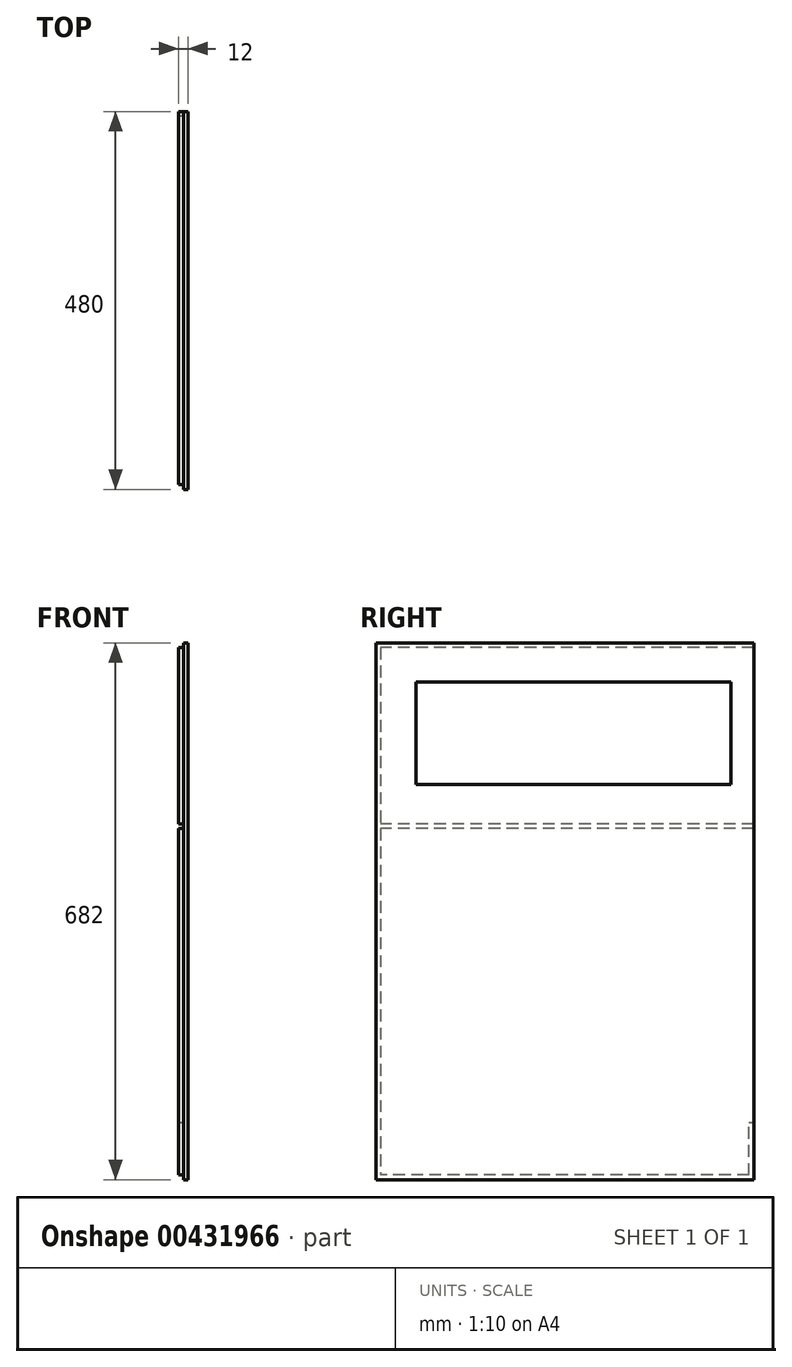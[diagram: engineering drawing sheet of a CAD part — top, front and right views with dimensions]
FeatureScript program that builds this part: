
annotation { "Feature Type Name" : "Feature", "Feature Type Description" : "" }
export const myFeature = defineFeature(function(context is Context, id is Id, definition is map)
    precondition{}
    {
        {
            var Q0;
            Q0=qCreatedBy(makeId("Right.planeOp"),FACE);
            var sketch = newSketch(context, id + "F0", { "sketchPlane" : qUnion([Q0])});
            skLineSegment(sketch, "E0.bottom", {"start": v(-240, 341) * mm, "end": v(240, 341) * mm});
            skLineSegment(sketch, "E0.top", {"start": v(-240, -341) * mm, "end": v(240, -341) * mm});
            skLineSegment(sketch, "E0.left", {"start": v(-240, 341) * mm, "end": v(-240, -341) * mm});
            skLineSegment(sketch, "E0.right", {"start": v(240, 341) * mm, "end": v(240, -341) * mm});
            skPoint(sketch, "E0.middle", {"position": v(0, 0) * mm});
            skSolve(sketch);
        }
        {
            var Q0;
            Q0=makeQuery(id+"F0.imprint","IMPRINT",FACE,{"disambiguationData":[TD([[makeQuery(id+"F0.imprint","IMPRINT",EDGE,{"derivedFrom":sQuery(id+"F0.wireOp",EDGE,"E0.bottom")}),-1.0]])]});
            extrude(context, id + "F1", {"entities" : qUnion([Q0]), "depth" : 12 * mm, "offsetDistance" : 25 * mm});
        }
        {
            var Q0;
            Q0=makeQuery(id+"F1.opExtrude","CAP_FACE",FACE,{"disambiguationData":[OSD([sQuery(id+"F0.wireOp",EDGE,"E0.bottom"),sQuery(id+"F0.wireOp",EDGE,"E0.top"),sQuery(id+"F0.wireOp",EDGE,"E0.left"),sQuery(id+"F0.wireOp",EDGE,"E0.right")])],"isStart":true});
            var sketch = newSketch(context, id + "F2", { "sketchPlane" : qUnion([Q0])});
            skLineSegment(sketch, "E1.bottom", {"start": v(240, 341) * mm, "end": v(234, 341) * mm});
            skLineSegment(sketch, "E1.top", {"start": v(240, -341) * mm, "end": v(234, -341) * mm});
            skLineSegment(sketch, "E1.left", {"start": v(240, 341) * mm, "end": v(240, -341) * mm});
            skLineSegment(sketch, "E1.right", {"start": v(234, 341) * mm, "end": v(234, -341) * mm});
            skSolve(sketch);
        }
        {
            var Q0;
            Q0=qSketchRegion(id+"F2",true);
            extrude(context, id + "F3", {"entities" : qUnion([Q0]), "operationType" : NewBodyOperationType.REMOVE, "oppositeDirection" : true, "depth" : 6 * mm, "offsetDistance" : 25 * mm});
        }
        {
            var Q0;
            {var subQ0=sQuery(id+"F0.wireOp",EDGE,"E0.bottom");var subQ1=sQuery(id+"F0.wireOp",EDGE,"E0.right");var subQ2=sQuery(id+"F0.wireOp",EDGE,"E0.top");Q0=makeQuery(id+"F3.boolean.opBoolean","SPLIT",FACE,{"disambiguationData":[TD([makeQuery(id+"F1.opExtrude","SWEPT_FACE",FACE,{"disambiguationData":[OSD([subQ1])]})])],"derivedFrom":makeQuery(id+"F1.opExtrude","CAP_FACE",FACE,{"disambiguationData":[OSD([subQ0,subQ2,sQuery(id+"F0.wireOp",EDGE,"E0.left"),subQ1])],"isStart":true})});}
            var sketch = newSketch(context, id + "F4", { "sketchPlane" : qUnion([Q0])});
            skLineSegment(sketch, "E2.bottom", {"start": v(-240, -335) * mm, "end": v(234, -335) * mm});
            skLineSegment(sketch, "E2.top", {"start": v(-240, -341) * mm, "end": v(234, -341) * mm});
            skLineSegment(sketch, "E2.left", {"start": v(-240, -335) * mm, "end": v(-240, -341) * mm});
            skLineSegment(sketch, "E2.right", {"start": v(234, -335) * mm, "end": v(234, -341) * mm});
            skSolve(sketch);
        }
        {
            var Q0;
            Q0=qSketchRegion(id+"F4",true);
            extrude(context, id + "F5", {"entities" : qUnion([Q0]), "operationType" : NewBodyOperationType.REMOVE, "oppositeDirection" : true, "depth" : 6 * mm, "offsetDistance" : 25 * mm});
        }
        {
            var Q0;
            {var subQ0=sQuery(id+"F0.wireOp",EDGE,"E0.bottom");var subQ1=sQuery(id+"F0.wireOp",EDGE,"E0.right");var subQ2=sQuery(id+"F0.wireOp",EDGE,"E0.top");Q0=makeQuery(id+"F3.boolean.opBoolean","SPLIT",FACE,{"disambiguationData":[TD([makeQuery(id+"F1.opExtrude","SWEPT_FACE",FACE,{"disambiguationData":[OSD([subQ1])]})])],"derivedFrom":makeQuery(id+"F1.opExtrude","CAP_FACE",FACE,{"disambiguationData":[OSD([subQ0,subQ2,sQuery(id+"F0.wireOp",EDGE,"E0.left"),subQ1])],"isStart":true})});}
            var sketch = newSketch(context, id + "F6", { "sketchPlane" : qUnion([Q0])});
            skLineSegment(sketch, "E3.bottom", {"start": v(-240, -335) * mm, "end": v(-234, -335) * mm});
            skLineSegment(sketch, "E3.top", {"start": v(-240, -269) * mm, "end": v(-234, -269) * mm});
            skLineSegment(sketch, "E3.left", {"start": v(-240, -335) * mm, "end": v(-240, -269) * mm});
            skLineSegment(sketch, "E3.right", {"start": v(-234, -335) * mm, "end": v(-234, -269) * mm});
            skSolve(sketch);
        }
        {
            var Q0;
            Q0=qSketchRegion(id+"F6",true);
            extrude(context, id + "F7", {"entities" : qUnion([Q0]), "operationType" : NewBodyOperationType.REMOVE, "oppositeDirection" : true, "depth" : 6 * mm, "offsetDistance" : 25 * mm});
        }
        {
            var Q0;
            {var subQ0=sQuery(id+"F0.wireOp",EDGE,"E0.bottom");var subQ1=sQuery(id+"F0.wireOp",EDGE,"E0.right");var subQ2=sQuery(id+"F0.wireOp",EDGE,"E0.top");Q0=makeQuery(id+"F3.boolean.opBoolean","SPLIT",FACE,{"disambiguationData":[TD([makeQuery(id+"F1.opExtrude","SWEPT_FACE",FACE,{"disambiguationData":[OSD([subQ1])]})])],"derivedFrom":makeQuery(id+"F1.opExtrude","CAP_FACE",FACE,{"disambiguationData":[OSD([subQ0,subQ2,sQuery(id+"F0.wireOp",EDGE,"E0.left"),subQ1])],"isStart":true})});}
            var sketch = newSketch(context, id + "F8", { "sketchPlane" : qUnion([Q0])});
            skLineSegment(sketch, "E4.bottom", {"start": v(-240, 105) * mm, "end": v(234, 105) * mm});
            skLineSegment(sketch, "E4.top", {"start": v(-240, 111) * mm, "end": v(234, 111) * mm});
            skLineSegment(sketch, "E4.left", {"start": v(-240, 105) * mm, "end": v(-240, 111) * mm});
            skLineSegment(sketch, "E4.right", {"start": v(234, 105) * mm, "end": v(234, 111) * mm});
            skSolve(sketch);
        }
        {
            var Q0;
            Q0=qSketchRegion(id+"F8",true);
            extrude(context, id + "F9", {"entities" : qUnion([Q0]), "operationType" : NewBodyOperationType.REMOVE, "oppositeDirection" : true, "depth" : 6 * mm, "offsetDistance" : 25 * mm});
        }
        {
            var Q0;
            {var subQ0=sQuery(id+"F0.wireOp",EDGE,"E0.bottom");var subQ1=makeQuery(id+"F1.opExtrude","SWEPT_FACE",FACE,{"disambiguationData":[OSD([subQ0])]});var subQ2=sQuery(id+"F0.wireOp",EDGE,"E0.right");var subQ3=makeQuery(id+"F1.opExtrude","SWEPT_FACE",FACE,{"disambiguationData":[OSD([subQ2])]});var subQ5=sQuery(id+"F0.wireOp",EDGE,"E0.top");Q0=makeQuery(id+"F9.boolean.opBoolean","SPLIT",FACE,{"disambiguationData":[TD([subQ1])],"derivedFrom":makeQuery(id+"F3.boolean.opBoolean","SPLIT",FACE,{"disambiguationData":[TD([subQ3])],"derivedFrom":makeQuery(id+"F1.opExtrude","CAP_FACE",FACE,{"disambiguationData":[OSD([subQ0,subQ5,sQuery(id+"F0.wireOp",EDGE,"E0.left"),subQ2])],"isStart":true})})});}
            var sketch = newSketch(context, id + "F10", { "sketchPlane" : qUnion([Q0])});
            skLineSegment(sketch, "E5.bottom", {"start": v(-211, 291) * mm, "end": v(189, 291) * mm});
            skLineSegment(sketch, "E5.top", {"start": v(-211, 161) * mm, "end": v(189, 161) * mm});
            skLineSegment(sketch, "E5.left", {"start": v(-211, 291) * mm, "end": v(-211, 161) * mm});
            skLineSegment(sketch, "E5.right", {"start": v(189, 291) * mm, "end": v(189, 161) * mm});
            skSolve(sketch);
        }
        {
            var Q0;
            Q0=qSketchRegion(id+"F10",true);
            extrude(context, id + "F11", {"entities" : qUnion([Q0]), "operationType" : NewBodyOperationType.REMOVE, "endBound" : BoundingType.UP_TO_NEXT, "oppositeDirection" : true, "depth" : 25 * mm});
        }
        {
            var Q0;
            {var subQ0=sQuery(id+"F0.wireOp",EDGE,"E0.bottom");var subQ1=makeQuery(id+"F1.opExtrude","SWEPT_FACE",FACE,{"disambiguationData":[OSD([subQ0])]});var subQ2=sQuery(id+"F0.wireOp",EDGE,"E0.right");var subQ3=makeQuery(id+"F1.opExtrude","SWEPT_FACE",FACE,{"disambiguationData":[OSD([subQ2])]});var subQ5=sQuery(id+"F0.wireOp",EDGE,"E0.top");Q0=makeQuery(id+"F9.boolean.opBoolean","SPLIT",FACE,{"disambiguationData":[TD([subQ1])],"derivedFrom":makeQuery(id+"F3.boolean.opBoolean","SPLIT",FACE,{"disambiguationData":[TD([subQ3])],"derivedFrom":makeQuery(id+"F1.opExtrude","CAP_FACE",FACE,{"disambiguationData":[OSD([subQ0,subQ5,sQuery(id+"F0.wireOp",EDGE,"E0.left"),subQ2])],"isStart":true})})});}
            var sketch = newSketch(context, id + "F12", { "sketchPlane" : qUnion([Q0])});
            skLineSegment(sketch, "E6.bottom", {"start": v(-240, 341) * mm, "end": v(234, 341) * mm});
            skLineSegment(sketch, "E6.top", {"start": v(-240, 335) * mm, "end": v(234, 335) * mm});
            skLineSegment(sketch, "E6.left", {"start": v(-240, 341) * mm, "end": v(-240, 335) * mm});
            skLineSegment(sketch, "E6.right", {"start": v(234, 341) * mm, "end": v(234, 335) * mm});
            skSolve(sketch);
        }
        {
            var Q0;
            Q0=qSketchRegion(id+"F12",true);
            extrude(context, id + "F13", {"entities" : qUnion([Q0]), "operationType" : NewBodyOperationType.REMOVE, "oppositeDirection" : true, "depth" : 6 * mm, "offsetDistance" : 25 * mm});
        }
    });
